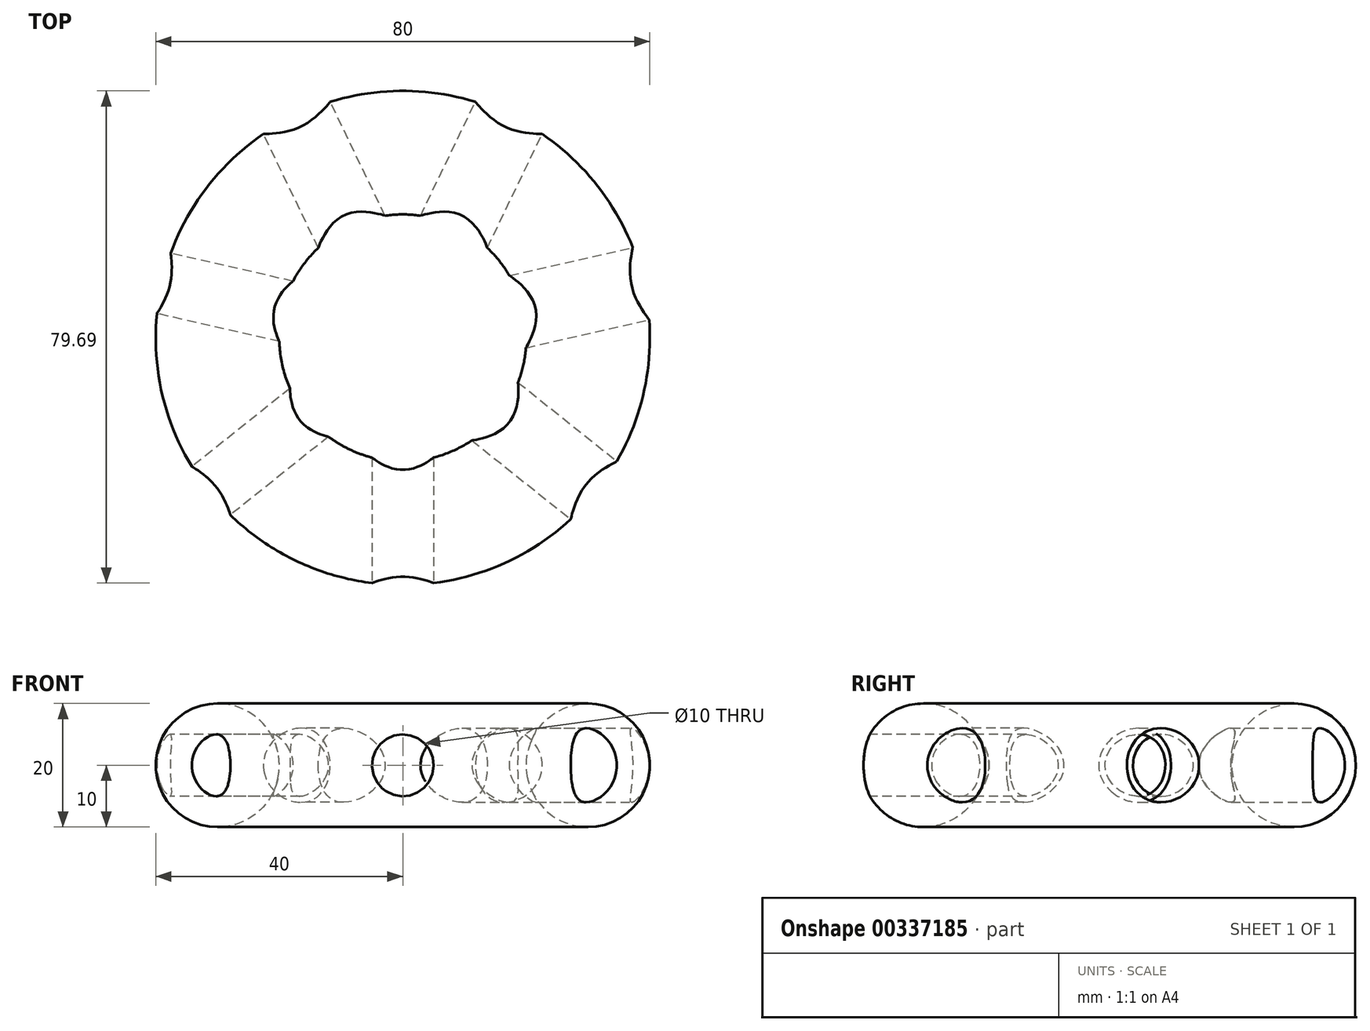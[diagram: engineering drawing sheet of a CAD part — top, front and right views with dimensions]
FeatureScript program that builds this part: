
annotation { "Feature Type Name" : "Feature", "Feature Type Description" : "" }
export const myFeature = defineFeature(function(context is Context, id is Id, definition is map)
    precondition{}
    {
        {
            var Q0;
            Q0=qCreatedBy(makeId("Front.planeOp"),FACE);
            var sketch = newSketch(context, id + "F0", { "sketchPlane" : qUnion([Q0])});
            skLineSegment(sketch, "E0", {"start": v(0, 41.4) * mm, "end": v(0, -26.53) * mm});
            skLineSegment(sketch, "E1", {"start": v(0, -26.53) * mm, "end": v(0, 0) * mm});
            skLineSegment(sketch, "E2", {"start": v(0, 0) * mm, "end": v(30, 0) * mm});
            skCircle(sketch, "E3", {"center": v(30, 0) * mm, "radius": 10 * mm});
            skSolve(sketch);
        }
        {
            var Q0;
            Q0=makeQuery(id+"F0.imprint","IMPRINT",FACE,{"disambiguationData":[TD([[makeQuery(id+"F0.imprint","IMPRINT",EDGE,{"derivedFrom":sQuery(id+"F0.wireOp",EDGE,"E3")}),1.0]])]});
            var Q1;
            Q1=sQuery(id+"F0.wireOp",EDGE,"E0");
            revolve(context, id + "F1", {"entities" : qUnion([Q0]), "axis" : qUnion([Q1]), "revolveType" : RevolveType.FULL});
        }
        {
            var Q0;
            Q0=qCreatedBy(makeId("Top.planeOp"),FACE);
            var sketch = newSketch(context, id + "F2", { "sketchPlane" : qUnion([Q0])});
            skLineSegment(sketch, "E4", {"start": v(0, 0) * mm, "end": v(0, -51.73) * mm});
            skLineSegment(sketch, "E5.1.0", {"start": v(0, 0) * mm, "end": v(40.44, -32.25) * mm});
            skLineSegment(sketch, "E5.2.0", {"start": v(0, 0) * mm, "end": v(50.43, 11.5) * mm});
            skLineSegment(sketch, "E5.3.0", {"start": v(0, 0) * mm, "end": v(22.44, 46.6) * mm});
            skLineSegment(sketch, "E5.4.0", {"start": v(0, 0) * mm, "end": v(-22.44, 46.6) * mm});
            skLineSegment(sketch, "E5.5.0", {"start": v(0, 0) * mm, "end": v(-50.43, 11.5) * mm});
            skLineSegment(sketch, "E5.6.0", {"start": v(0, 0) * mm, "end": v(-40.44, -32.25) * mm});
            skPoint(sketch, "E5.center", {"position": v(0, 0) * mm});
            skLineSegment(sketch, "E6.anchor1", {"start": v(0, 0) * mm, "end": v(0, -51.73) * mm, "construction": true});
            skLineSegment(sketch, "E6.anchor2", {"start": v(0, 0) * mm, "end": v(0, -51.73) * mm, "construction": true});
            skSolve(sketch);
        }
        {
            var Q0;
            Q0=qCreatedBy(makeId("Front.planeOp"),FACE);
            var sketch = newSketch(context, id + "F3", { "sketchPlane" : qUnion([Q0])});
            skCircle(sketch, "E7", {"center": v(0, 0) * mm, "radius": 5 * mm});
            skSolve(sketch);
        }
        {
            var Q0;
            Q0=makeQuery(id+"F3.imprint","IMPRINT",FACE,{"disambiguationData":[TD([[makeQuery(id+"F3.imprint","IMPRINT",EDGE,{"derivedFrom":sQuery(id+"F3.wireOp",EDGE,"E7")}),1.0]])]});
            var Q1;
            Q1=sQuery(id+"F2.wireOp",EDGE,"E4");
            sweep(context, id + "F4", {"operationType" : NewBodyOperationType.REMOVE, "profiles" : qUnion([Q0]), "path" : qUnion([Q1])});
        }
        {
            var Q0;
            Q0=sQuery(id+"F2.wireOp",EDGE,"E5.6.0");
            var Q1;
            Q1=sQuery(id+"F2.wireOp",VERTEX,"E5.center");
            cPlane(context, id + "F5", {"entities" : qUnion([Q0, Q1]), "cplaneType" : CPlaneType.LINE_POINT, "offset" : 25 * mm, "width" : 150 * mm, "height" : 150 * mm});
        }
        {
            var Q0;
            Q0=qCreatedBy(id+"F5.planeOp",FACE);
            var sketch = newSketch(context, id + "F6", { "sketchPlane" : qUnion([Q0])});
            skCircle(sketch, "E8", {"center": v(0, 0) * mm, "radius": 5 * mm});
            skSolve(sketch);
        }
        {
            var Q0;
            Q0=makeQuery(id+"F6.imprint","IMPRINT",FACE,{"disambiguationData":[TD([[makeQuery(id+"F6.imprint","IMPRINT",EDGE,{"derivedFrom":sQuery(id+"F6.wireOp",EDGE,"E8")}),1.0]])]});
            var Q1;
            Q1=sQuery(id+"F2.wireOp",EDGE,"E5.6.0");
            sweep(context, id + "F7", {"operationType" : NewBodyOperationType.REMOVE, "profiles" : qUnion([Q0]), "path" : qUnion([Q1])});
        }
        {
            var Q0;
            Q0=sQuery(id+"F2.wireOp",VERTEX,"E5.center");
            var Q1;
            Q1=sQuery(id+"F2.wireOp",EDGE,"E5.5.0");
            cPlane(context, id + "F8", {"entities" : qUnion([Q0, Q1]), "cplaneType" : CPlaneType.LINE_POINT, "offset" : 25 * mm, "width" : 150 * mm, "height" : 150 * mm});
        }
        {
            var Q0;
            Q0=qCreatedBy(id+"F8.planeOp",FACE);
            var sketch = newSketch(context, id + "F9", { "sketchPlane" : qUnion([Q0])});
            skCircle(sketch, "E9", {"center": v(0, 0) * mm, "radius": 5 * mm});
            skSolve(sketch);
        }
        {
            var Q0;
            Q0=makeQuery(id+"F9.imprint","IMPRINT",FACE,{"disambiguationData":[TD([[makeQuery(id+"F9.imprint","IMPRINT",EDGE,{"derivedFrom":sQuery(id+"F9.wireOp",EDGE,"E9")}),1.0]])]});
            var Q1;
            Q1=sQuery(id+"F2.wireOp",EDGE,"E5.5.0");
            sweep(context, id + "F10", {"operationType" : NewBodyOperationType.REMOVE, "profiles" : qUnion([Q0]), "path" : qUnion([Q1])});
        }
        {
            var Q0;
            Q0=sQuery(id+"F2.wireOp",VERTEX,"E5.center");
            var Q1;
            Q1=sQuery(id+"F2.wireOp",EDGE,"E5.4.0");
            cPlane(context, id + "F11", {"entities" : qUnion([Q0, Q1]), "cplaneType" : CPlaneType.LINE_POINT, "offset" : 25 * mm, "width" : 150 * mm, "height" : 150 * mm});
        }
        {
            var Q0;
            Q0=qCreatedBy(id+"F11.planeOp",FACE);
            var sketch = newSketch(context, id + "F12", { "sketchPlane" : qUnion([Q0])});
            skCircle(sketch, "E10", {"center": v(0, 0) * mm, "radius": 6 * mm});
            skSolve(sketch);
        }
        {
            var Q0;
            Q0=makeQuery(id+"F12.imprint","IMPRINT",FACE,{"disambiguationData":[TD([[makeQuery(id+"F12.imprint","IMPRINT",EDGE,{"derivedFrom":sQuery(id+"F12.wireOp",EDGE,"E10")}),1.0]])]});
            var Q1;
            Q1=sQuery(id+"F2.wireOp",EDGE,"E5.4.0");
            sweep(context, id + "F13", {"operationType" : NewBodyOperationType.REMOVE, "profiles" : qUnion([Q0]), "path" : qUnion([Q1])});
        }
        {
            var Q0;
            Q0=sQuery(id+"F2.wireOp",VERTEX,"E5.center");
            var Q1;
            Q1=sQuery(id+"F2.wireOp",EDGE,"E5.3.0");
            cPlane(context, id + "F14", {"entities" : qUnion([Q0, Q1]), "cplaneType" : CPlaneType.LINE_POINT, "offset" : 25 * mm, "width" : 150 * mm, "height" : 150 * mm});
        }
        {
            var Q0;
            Q0=qCreatedBy(id+"F14.planeOp",FACE);
            var sketch = newSketch(context, id + "F15", { "sketchPlane" : qUnion([Q0])});
            skCircle(sketch, "E11", {"center": v(0, 0) * mm, "radius": 6 * mm});
            skSolve(sketch);
        }
        {
            var Q0;
            Q0=makeQuery(id+"F15.imprint","IMPRINT",FACE,{"disambiguationData":[TD([[makeQuery(id+"F15.imprint","IMPRINT",EDGE,{"derivedFrom":sQuery(id+"F15.wireOp",EDGE,"E11")}),1.0]])]});
            var Q1;
            Q1=sQuery(id+"F2.wireOp",EDGE,"E5.3.0");
            sweep(context, id + "F16", {"operationType" : NewBodyOperationType.REMOVE, "profiles" : qUnion([Q0]), "path" : qUnion([Q1])});
        }
        {
            var Q0;
            Q0=sQuery(id+"F2.wireOp",VERTEX,"E5.center");
            var Q1;
            Q1=sQuery(id+"F2.wireOp",EDGE,"E5.2.0");
            cPlane(context, id + "F17", {"entities" : qUnion([Q0, Q1]), "cplaneType" : CPlaneType.LINE_POINT, "offset" : 25 * mm, "width" : 150 * mm, "height" : 150 * mm});
        }
        {
            var Q0;
            Q0=qCreatedBy(id+"F17.planeOp",FACE);
            var sketch = newSketch(context, id + "F18", { "sketchPlane" : qUnion([Q0])});
            skCircle(sketch, "E12", {"center": v(0, 0) * mm, "radius": 6 * mm});
            skSolve(sketch);
        }
        {
            var Q0;
            Q0=makeQuery(id+"F18.imprint","IMPRINT",FACE,{"disambiguationData":[TD([[makeQuery(id+"F18.imprint","IMPRINT",EDGE,{"derivedFrom":sQuery(id+"F18.wireOp",EDGE,"E12")}),1.0]])]});
            var Q1;
            Q1=sQuery(id+"F2.wireOp",EDGE,"E5.2.0");
            sweep(context, id + "F19", {"operationType" : NewBodyOperationType.REMOVE, "profiles" : qUnion([Q0]), "path" : qUnion([Q1])});
        }
        {
            var Q0;
            Q0=sQuery(id+"F2.wireOp",VERTEX,"E5.center");
            var Q1;
            Q1=sQuery(id+"F2.wireOp",EDGE,"E5.1.0");
            cPlane(context, id + "F20", {"entities" : qUnion([Q0, Q1]), "cplaneType" : CPlaneType.LINE_POINT, "offset" : 25 * mm, "width" : 150 * mm, "height" : 150 * mm});
        }
        {
            var Q0;
            Q0=qCreatedBy(id+"F20.planeOp",FACE);
            var sketch = newSketch(context, id + "F21", { "sketchPlane" : qUnion([Q0])});
            skCircle(sketch, "E13", {"center": v(0, 0) * mm, "radius": 6 * mm});
            skSolve(sketch);
        }
        {
            var Q0;
            Q0=makeQuery(id+"F21.imprint","IMPRINT",FACE,{"disambiguationData":[TD([[makeQuery(id+"F21.imprint","IMPRINT",EDGE,{"derivedFrom":sQuery(id+"F21.wireOp",EDGE,"E13")}),1.0]])]});
            var Q1;
            Q1=sQuery(id+"F2.wireOp",EDGE,"E5.1.0");
            sweep(context, id + "F22", {"operationType" : NewBodyOperationType.REMOVE, "profiles" : qUnion([Q0]), "path" : qUnion([Q1])});
        }
    });
